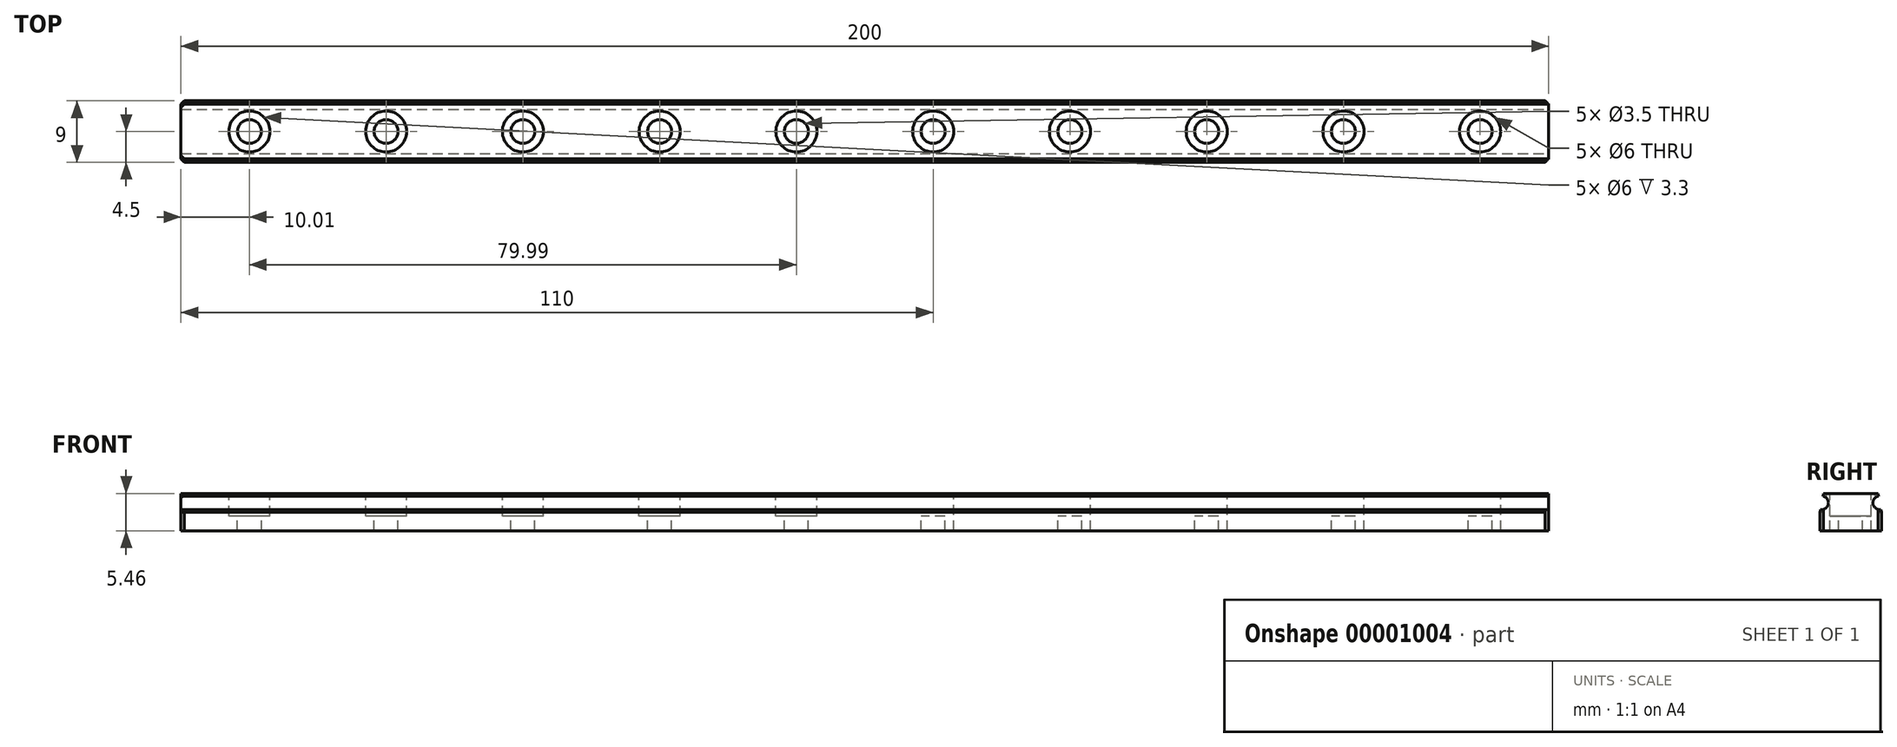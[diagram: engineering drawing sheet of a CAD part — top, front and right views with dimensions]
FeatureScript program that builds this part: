
annotation { "Feature Type Name" : "Feature", "Feature Type Description" : "" }
export const myFeature = defineFeature(function(context is Context, id is Id, definition is map)
    precondition{}
    {
        {
            var Q0;
            Q0=qCreatedBy(makeId("Top.planeOp"),FACE);
            var sketch = newSketch(context, id + "F0", { "sketchPlane" : qUnion([Q0])});
            skLineSegment(sketch, "E0.bottom", {"start": v(100, -4.5) * mm, "end": v(-100, -4.5) * mm});
            skLineSegment(sketch, "E0.top", {"start": v(100, 4.5) * mm, "end": v(-100, 4.5) * mm});
            skLineSegment(sketch, "E0.left", {"start": v(100, -4.5) * mm, "end": v(100, 4.5) * mm});
            skLineSegment(sketch, "E0.right", {"start": v(-100, -4.5) * mm, "end": v(-100, 4.5) * mm});
            skCircle(sketch, "E1", {"center": v(-10, 0) * mm, "radius": 1.75 * mm});
            skCircle(sketch, "E2", {"center": v(-30, 0) * mm, "radius": 1.75 * mm});
            skCircle(sketch, "E3", {"center": v(-50, 0) * mm, "radius": 1.75 * mm});
            skCircle(sketch, "E4", {"center": v(-10, 0) * mm, "radius": 3 * mm});
            skCircle(sketch, "E5", {"center": v(-30, 0) * mm, "radius": 3 * mm});
            skCircle(sketch, "E6", {"center": v(-50, 0) * mm, "radius": 3 * mm});
            skCircle(sketch, "E7", {"center": v(-70, 0) * mm, "radius": 1.75 * mm});
            skCircle(sketch, "E8", {"center": v(-70, 0) * mm, "radius": 3 * mm});
            skCircle(sketch, "E9", {"center": v(-89.99, 0) * mm, "radius": 3 * mm});
            skCircle(sketch, "E10", {"center": v(-89.99, 0) * mm, "radius": 1.75 * mm});
            skLineSegment(sketch, "E11", {"start": v(0, 0) * mm, "end": v(0, 8.25) * mm, "construction": true});
            skCircle(sketch, "E12.0.MirrorC", {"center": v(89.99, 0) * mm, "radius": 1.75 * mm});
            skCircle(sketch, "E13.0.MirrorC", {"center": v(89.99, 0) * mm, "radius": 3 * mm});
            skCircle(sketch, "E14.0.MirrorC", {"center": v(10, 0) * mm, "radius": 1.75 * mm});
            skCircle(sketch, "E15.0.MirrorC", {"center": v(30, 0) * mm, "radius": 1.75 * mm});
            skCircle(sketch, "E16.0.MirrorC", {"center": v(50, 0) * mm, "radius": 1.75 * mm});
            skCircle(sketch, "E17.0.MirrorC", {"center": v(70, 0) * mm, "radius": 1.75 * mm});
            skCircle(sketch, "E18.0.MirrorC", {"center": v(70, 0) * mm, "radius": 3 * mm});
            skCircle(sketch, "E19.0.MirrorC", {"center": v(50, 0) * mm, "radius": 3 * mm});
            skCircle(sketch, "E20.0.MirrorC", {"center": v(30, 0) * mm, "radius": 3 * mm});
            skCircle(sketch, "E21.0.MirrorC", {"center": v(10, 0) * mm, "radius": 3 * mm});
            skSolve(sketch);
        }
        {
            var Q0;
            Q0=makeQuery(id+"F0.imprint","IMPRINT",FACE,{"disambiguationData":[TD([[makeQuery(id+"F0.imprint","IMPRINT",EDGE,{"derivedFrom":sQuery(id+"F0.wireOp",EDGE,"E0.bottom")}),-1.0]])]});
            var Q1;
            Q1=makeQuery(id+"F0.imprint","IMPRINT",FACE,{"disambiguationData":[TD([[makeQuery(id+"F0.imprint","IMPRINT",EDGE,{"derivedFrom":sQuery(id+"F0.wireOp",EDGE,"E1")}),-1.0]])]});
            var Q2;
            Q2=makeQuery(id+"F0.imprint","IMPRINT",FACE,{"disambiguationData":[TD([[makeQuery(id+"F0.imprint","IMPRINT",EDGE,{"derivedFrom":sQuery(id+"F0.wireOp",EDGE,"761e571b-ad26-4600-99ce-cd4df0bb8774")}),-1.0]])]});
            var Q3;
            Q3=makeQuery(id+"F0.imprint","IMPRINT",FACE,{"disambiguationData":[TD([[makeQuery(id+"F0.imprint","IMPRINT",EDGE,{"derivedFrom":sQuery(id+"F0.wireOp",EDGE,"30e0f528-dbd1-4d2e-a73f-525115ea55a2")}),-1.0]])]});
            var Q4;
            Q4=makeQuery(id+"F0.imprint","IMPRINT",FACE,{"disambiguationData":[TD([[makeQuery(id+"F0.imprint","IMPRINT",EDGE,{"derivedFrom":sQuery(id+"F0.wireOp",EDGE,"E2")}),-1.0]])]});
            var Q5;
            Q5=makeQuery(id+"F0.imprint","IMPRINT",FACE,{"disambiguationData":[TD([[makeQuery(id+"F0.imprint","IMPRINT",EDGE,{"derivedFrom":sQuery(id+"F0.wireOp",EDGE,"E3")}),-1.0]])]});
            var Q6;
            Q6=makeQuery(id+"F0.imprint","IMPRINT",FACE,{"disambiguationData":[TD([[makeQuery(id+"F0.imprint","IMPRINT",EDGE,{"derivedFrom":sQuery(id+"F0.wireOp",EDGE,"E7")}),-1.0]])]});
            var Q7;
            Q7=makeQuery(id+"F0.imprint","IMPRINT",FACE,{"disambiguationData":[TD([[makeQuery(id+"F0.imprint","IMPRINT",EDGE,{"derivedFrom":sQuery(id+"F0.wireOp",EDGE,"d70bcf1e-7b07-4f55-aaf2-f84dbc7d1e34")}),-1.0]])]});
            var Q8;
            Q8=makeQuery(id+"F0.imprint","IMPRINT",FACE,{"disambiguationData":[TD([[makeQuery(id+"F0.imprint","IMPRINT",EDGE,{"derivedFrom":sQuery(id+"F0.wireOp",EDGE,"4aa4544c-dbd7-424f-be88-efd2949ea764")}),-1.0]])]});
            var Q9;
            Q9=makeQuery(id+"F0.imprint","IMPRINT",FACE,{"disambiguationData":[TD([[makeQuery(id+"F0.imprint","IMPRINT",EDGE,{"derivedFrom":sQuery(id+"F0.wireOp",EDGE,"E9")}),1.0]])]});
            var Q10;
            Q10=makeQuery(id+"F0.imprint","IMPRINT",FACE,{"disambiguationData":[TD([[makeQuery(id+"F0.imprint","IMPRINT",EDGE,{"derivedFrom":sQuery(id+"F0.wireOp",EDGE,"E14.0.MirrorC")}),1.0]])]});
            var Q11;
            Q11=makeQuery(id+"F0.imprint","IMPRINT",FACE,{"disambiguationData":[TD([[makeQuery(id+"F0.imprint","IMPRINT",EDGE,{"derivedFrom":sQuery(id+"F0.wireOp",EDGE,"E15.0.MirrorC")}),1.0]])]});
            var Q12;
            Q12=makeQuery(id+"F0.imprint","IMPRINT",FACE,{"disambiguationData":[TD([[makeQuery(id+"F0.imprint","IMPRINT",EDGE,{"derivedFrom":sQuery(id+"F0.wireOp",EDGE,"E16.0.MirrorC")}),1.0]])]});
            var Q13;
            Q13=makeQuery(id+"F0.imprint","IMPRINT",FACE,{"disambiguationData":[TD([[makeQuery(id+"F0.imprint","IMPRINT",EDGE,{"derivedFrom":sQuery(id+"F0.wireOp",EDGE,"E17.0.MirrorC")}),1.0]])]});
            var Q14;
            Q14=makeQuery(id+"F0.imprint","IMPRINT",FACE,{"disambiguationData":[TD([[makeQuery(id+"F0.imprint","IMPRINT",EDGE,{"derivedFrom":sQuery(id+"F0.wireOp",EDGE,"E12.0.MirrorC")}),1.0]])]});
            extrude(context, id + "F1", {"entities" : qUnion([Q0, Q1, Q2, Q3, Q4, Q5, Q6, Q7, Q8, Q9, Q10, Q11, Q12, Q13, Q14]), "oppositeDirection" : true, "depth" : 5.46 * mm});
        }
        {
            var Q0;
            Q0=makeQuery(id+"F0.imprint","IMPRINT",FACE,{"disambiguationData":[TD([[makeQuery(id+"F0.imprint","IMPRINT",EDGE,{"derivedFrom":sQuery(id+"F0.wireOp",EDGE,"E7")}),-1.0]])]});
            var Q1;
            Q1=makeQuery(id+"F0.imprint","IMPRINT",FACE,{"disambiguationData":[TD([[makeQuery(id+"F0.imprint","IMPRINT",EDGE,{"derivedFrom":sQuery(id+"F0.wireOp",EDGE,"E3")}),-1.0]])]});
            var Q2;
            Q2=makeQuery(id+"F0.imprint","IMPRINT",FACE,{"disambiguationData":[TD([[makeQuery(id+"F0.imprint","IMPRINT",EDGE,{"derivedFrom":sQuery(id+"F0.wireOp",EDGE,"E2")}),-1.0]])]});
            var Q3;
            Q3=makeQuery(id+"F0.imprint","IMPRINT",FACE,{"disambiguationData":[TD([[makeQuery(id+"F0.imprint","IMPRINT",EDGE,{"derivedFrom":sQuery(id+"F0.wireOp",EDGE,"E1")}),-1.0]])]});
            var Q4;
            Q4=makeQuery(id+"F0.imprint","IMPRINT",FACE,{"disambiguationData":[TD([[makeQuery(id+"F0.imprint","IMPRINT",EDGE,{"derivedFrom":sQuery(id+"F0.wireOp",EDGE,"761e571b-ad26-4600-99ce-cd4df0bb8774")}),-1.0]])]});
            var Q5;
            Q5=makeQuery(id+"F0.imprint","IMPRINT",FACE,{"disambiguationData":[TD([[makeQuery(id+"F0.imprint","IMPRINT",EDGE,{"derivedFrom":sQuery(id+"F0.wireOp",EDGE,"30e0f528-dbd1-4d2e-a73f-525115ea55a2")}),-1.0]])]});
            var Q6;
            Q6=makeQuery(id+"F0.imprint","IMPRINT",FACE,{"disambiguationData":[TD([[makeQuery(id+"F0.imprint","IMPRINT",EDGE,{"derivedFrom":sQuery(id+"F0.wireOp",EDGE,"d70bcf1e-7b07-4f55-aaf2-f84dbc7d1e34")}),-1.0]])]});
            var Q7;
            Q7=makeQuery(id+"F0.imprint","IMPRINT",FACE,{"disambiguationData":[TD([[makeQuery(id+"F0.imprint","IMPRINT",EDGE,{"derivedFrom":sQuery(id+"F0.wireOp",EDGE,"4aa4544c-dbd7-424f-be88-efd2949ea764")}),-1.0]])]});
            var Q8;
            Q8=makeQuery(id+"F0.imprint","IMPRINT",FACE,{"disambiguationData":[TD([[makeQuery(id+"F0.imprint","IMPRINT",EDGE,{"derivedFrom":sQuery(id+"F0.wireOp",EDGE,"E14.0.MirrorC")}),1.0]])]});
            var Q9;
            Q9=makeQuery(id+"F0.imprint","IMPRINT",FACE,{"disambiguationData":[TD([[makeQuery(id+"F0.imprint","IMPRINT",EDGE,{"derivedFrom":sQuery(id+"F0.wireOp",EDGE,"E15.0.MirrorC")}),1.0]])]});
            var Q10;
            Q10=makeQuery(id+"F0.imprint","IMPRINT",FACE,{"disambiguationData":[TD([[makeQuery(id+"F0.imprint","IMPRINT",EDGE,{"derivedFrom":sQuery(id+"F0.wireOp",EDGE,"E16.0.MirrorC")}),1.0]])]});
            var Q11;
            Q11=makeQuery(id+"F0.imprint","IMPRINT",FACE,{"disambiguationData":[TD([[makeQuery(id+"F0.imprint","IMPRINT",EDGE,{"derivedFrom":sQuery(id+"F0.wireOp",EDGE,"E17.0.MirrorC")}),1.0]])]});
            var Q12;
            Q12=makeQuery(id+"F0.imprint","IMPRINT",FACE,{"disambiguationData":[TD([[makeQuery(id+"F0.imprint","IMPRINT",EDGE,{"derivedFrom":sQuery(id+"F0.wireOp",EDGE,"E12.0.MirrorC")}),1.0]])]});
            var Q13;
            Q13=makeQuery(id+"F0.imprint","IMPRINT",FACE,{"disambiguationData":[TD([[makeQuery(id+"F0.imprint","IMPRINT",EDGE,{"derivedFrom":sQuery(id+"F0.wireOp",EDGE,"E9")}),1.0]])]});
            extrude(context, id + "F2", {"entities" : qUnion([Q0, Q1, Q2, Q3, Q4, Q5, Q6, Q7, Q8, Q9, Q10, Q11, Q12, Q13]), "operationType" : NewBodyOperationType.REMOVE, "oppositeDirection" : true, "depth" : 3.3 * mm});
        }
        {
            var Q0;
            Q0=makeQuery(id+"F1.opExtrude","SWEPT_FACE",FACE,{"disambiguationData":[OSD([sQuery(id+"F0.wireOp",EDGE,"E0.left")])]});
            var sketch = newSketch(context, id + "F3", { "sketchPlane" : qUnion([Q0])});
            skLineSegment(sketch, "E22", {"start": v(-4, 0) * mm, "end": v(-4.07, -0.38) * mm});
            skLineSegment(sketch, "E23", {"start": v(4.5, -2.73) * mm, "end": v(4.43, -2.35) * mm});
            skArc(sketch, "E24", {"start": v(-4.43, -2.35) * mm, "mid": v(-3.27, -1.55) * mm, "end": v(-4.07, -0.38) * mm});
            skArc(sketch, "E25", {"start": v(4.07, -0.38) * mm, "mid": v(3.27, -1.55) * mm, "end": v(4.43, -2.35) * mm});
            skLineSegment(sketch, "E26.trimOffspring", {"start": v(-4.43, -2.35) * mm, "end": v(-4.5, -2.73) * mm});
            skLineSegment(sketch, "E27.trimOffspring", {"start": v(4.07, -0.38) * mm, "end": v(4, 0) * mm});
            skLineSegment(sketch, "E28", {"start": v(-4, 0) * mm, "end": v(-4.5, 0) * mm});
            skLineSegment(sketch, "E29", {"start": v(-4.5, 0) * mm, "end": v(-4.5, -2.73) * mm});
            skLineSegment(sketch, "E30", {"start": v(4, 0) * mm, "end": v(4.5, 0) * mm});
            skLineSegment(sketch, "E31", {"start": v(4.5, 0) * mm, "end": v(4.5, -2.73) * mm});
            skSolve(sketch);
        }
        {
            var Q0;
            {Q0=qUnion([makeQuery(id+"F3.imprint","IMPRINT",FACE,{"disambiguationData":[TD([[makeQuery(id+"F3.imprint","IMPRINT",EDGE,{"derivedFrom":sQuery(id+"F3.wireOp",EDGE,"E22")}),-1.0]])]}),makeQuery(id+"F3.imprint","IMPRINT",FACE,{"disambiguationData":[TD([[makeQuery(id+"F3.imprint","IMPRINT",EDGE,{"derivedFrom":sQuery(id+"F3.wireOp",EDGE,"E23")}),-1.0]])]})]);}
            extrude(context, id + "F4", {"entities" : qUnion([Q0]), "operationType" : NewBodyOperationType.REMOVE, "endBound" : BoundingType.THROUGH_ALL, "oppositeDirection" : true, "depth" : 25.4 * mm});
        }
        {
            var Q0;
            Q0=makeQuery(id+"F4.boolean.opBoolean","COPY",EDGE,{"derivedFrom":makeQuery(id+"F4.opExtrude","CAP_EDGE",EDGE,{"disambiguationData":[OSD([sQuery(id+"F3.wireOp",EDGE,"E27.trimOffspring")])],"isStart":true})});
            var Q1;
            Q1=makeQuery(id+"F4.boolean.opBoolean","COPY",EDGE,{"derivedFrom":makeQuery(id+"F4.opExtrude","CAP_EDGE",EDGE,{"disambiguationData":[OSD([sQuery(id+"F3.wireOp",EDGE,"E23")])],"isStart":true})});
            var Q2;
            Q2=makeQuery(id+"F1.opExtrude","SWEPT_EDGE",EDGE,{"disambiguationData":[OSD([sQuery(id+"F0.wireOp",EDGE,"E0.top"),sQuery(id+"F0.wireOp",EDGE,"E0.left")])]});
            var Q3;
            Q3=makeQuery(id+"F1.opExtrude","SWEPT_EDGE",EDGE,{"disambiguationData":[OSD([sQuery(id+"F0.wireOp",EDGE,"E0.bottom"),sQuery(id+"F0.wireOp",EDGE,"E0.left")])]});
            var Q4;
            Q4=makeQuery(id+"F4.boolean.opBoolean","COPY",EDGE,{"derivedFrom":makeQuery(id+"F4.opExtrude","CAP_EDGE",EDGE,{"disambiguationData":[OSD([sQuery(id+"F3.wireOp",EDGE,"E26.trimOffspring")])],"isStart":true})});
            var Q5;
            Q5=makeQuery(id+"F4.boolean.opBoolean","COPY",EDGE,{"derivedFrom":makeQuery(id+"F4.opExtrude","CAP_EDGE",EDGE,{"disambiguationData":[OSD([sQuery(id+"F3.wireOp",EDGE,"E22")])],"isStart":true})});
            var Q6;
            Q6=makeQuery(id+"F1.opExtrude","SWEPT_EDGE",EDGE,{"disambiguationData":[OSD([sQuery(id+"F0.wireOp",EDGE,"E0.bottom"),sQuery(id+"F0.wireOp",EDGE,"E0.right")])]});
            var Q7;
            Q7=makeQuery(id+"F4.boolean.opBoolean","INTERSECT",EDGE,{"derivedFrom":[makeQuery(id+"F1.opExtrude","SWEPT_FACE",FACE,{"disambiguationData":[OSD([sQuery(id+"F0.wireOp",EDGE,"E0.right")])]}),makeQuery(id+"F4.opExtrude","SWEPT_FACE",FACE,{"disambiguationData":[OSD([sQuery(id+"F3.wireOp",EDGE,"E26.trimOffspring")])]})]});
            var Q8;
            Q8=makeQuery(id+"F4.boolean.opBoolean","INTERSECT",EDGE,{"derivedFrom":[makeQuery(id+"F1.opExtrude","SWEPT_FACE",FACE,{"disambiguationData":[OSD([sQuery(id+"F0.wireOp",EDGE,"E0.right")])]}),makeQuery(id+"F4.opExtrude","SWEPT_FACE",FACE,{"disambiguationData":[OSD([sQuery(id+"F3.wireOp",EDGE,"E22")])]})]});
            var Q9;
            Q9=makeQuery(id+"F4.boolean.opBoolean","INTERSECT",EDGE,{"derivedFrom":[makeQuery(id+"F1.opExtrude","SWEPT_FACE",FACE,{"disambiguationData":[OSD([sQuery(id+"F0.wireOp",EDGE,"E0.right")])]}),makeQuery(id+"F4.opExtrude","SWEPT_FACE",FACE,{"disambiguationData":[OSD([sQuery(id+"F3.wireOp",EDGE,"E27.trimOffspring")])]})]});
            var Q10;
            Q10=makeQuery(id+"F1.opExtrude","SWEPT_EDGE",EDGE,{"disambiguationData":[OSD([sQuery(id+"F0.wireOp",EDGE,"E0.top"),sQuery(id+"F0.wireOp",EDGE,"E0.right")])]});
            var Q11;
            Q11=makeQuery(id+"F4.boolean.opBoolean","INTERSECT",EDGE,{"derivedFrom":[makeQuery(id+"F1.opExtrude","SWEPT_FACE",FACE,{"disambiguationData":[OSD([sQuery(id+"F0.wireOp",EDGE,"E0.right")])]}),makeQuery(id+"F4.opExtrude","SWEPT_FACE",FACE,{"disambiguationData":[OSD([sQuery(id+"F3.wireOp",EDGE,"E23")])]})]});
            chamfer(context, id + "F5", {"entities" : qUnion([Q0, Q1, Q2, Q3, Q4, Q5, Q6, Q7, Q8, Q9, Q10, Q11]), "width" : 0.5 * mm, "tangentPropagation" : true});
        }
    });
